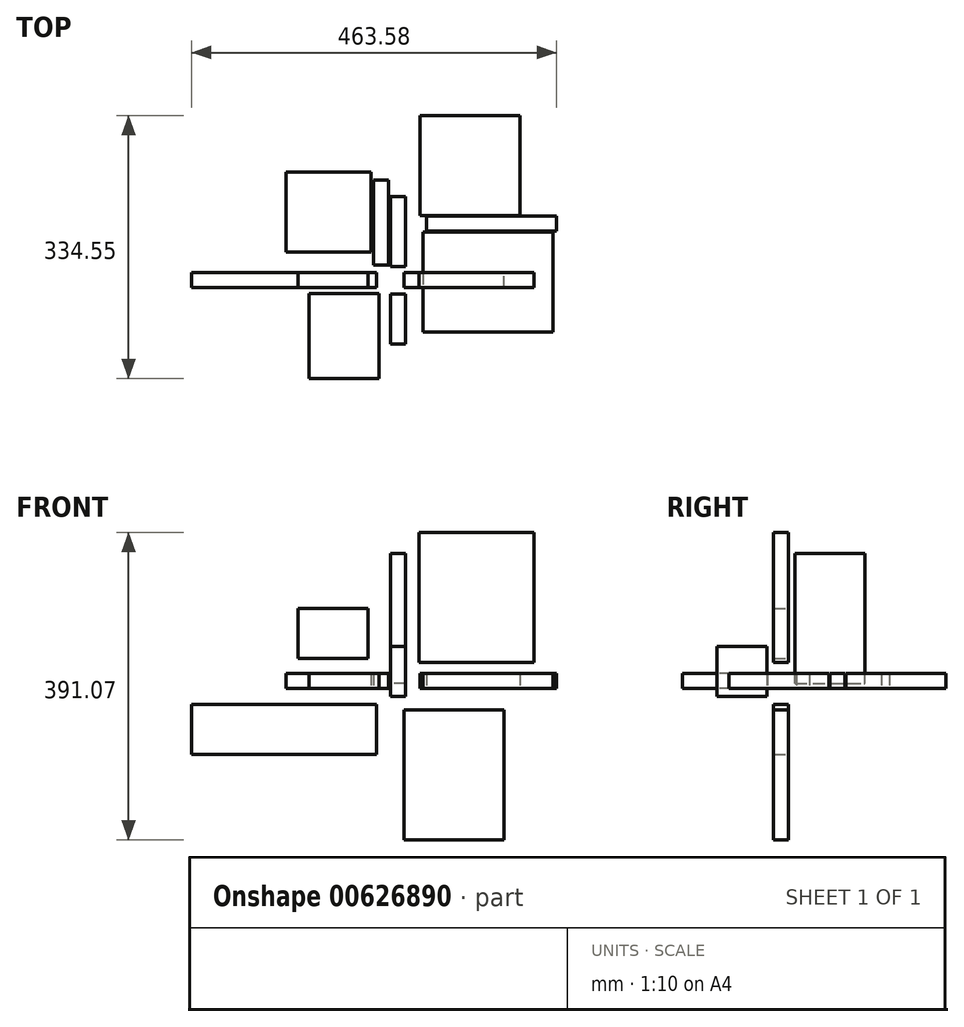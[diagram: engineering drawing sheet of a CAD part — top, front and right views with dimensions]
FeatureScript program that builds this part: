
annotation { "Feature Type Name" : "Feature", "Feature Type Description" : "" }
export const myFeature = defineFeature(function(context is Context, id is Id, definition is map)
    precondition{}
    {
        {
            var Q0;
            Q0=qCreatedBy(makeId("Right.planeOp"),FACE);
            var sketch = newSketch(context, id + "F0", { "sketchPlane" : qUnion([Q0])});
            skLineSegment(sketch, "E0.bottom", {"start": v(8.17, 6.2) * mm, "end": v(97.07, 6.2) * mm});
            skLineSegment(sketch, "E0.top", {"start": v(8.17, 171.3) * mm, "end": v(97.07, 171.3) * mm});
            skLineSegment(sketch, "E0.left", {"start": v(8.17, 6.2) * mm, "end": v(8.17, 171.3) * mm});
            skLineSegment(sketch, "E0.right", {"start": v(97.07, 6.2) * mm, "end": v(97.07, 171.3) * mm});
            skSolve(sketch);
        }
        {
            var Q0;
            Q0 = qSketchRegion(id + "F0", true);
            extrude(context, id + "F1", {"entities" : qUnion([Q0]), "depth" : 19.05 * mm, "offsetDistance" : 25.4 * mm});
        }
        {
            var Q0;
            Q0=qCreatedBy(makeId("Right.planeOp"),FACE);
            var sketch = newSketch(context, id + "F2", { "sketchPlane" : qUnion([Q0])});
            skLineSegment(sketch, "E1.bottom", {"start": v(-27.28, 53.43) * mm, "end": v(-90.78, 53.43) * mm});
            skLineSegment(sketch, "E1.top", {"start": v(-27.28, -10.07) * mm, "end": v(-90.78, -10.07) * mm});
            skLineSegment(sketch, "E1.left", {"start": v(-27.28, 53.43) * mm, "end": v(-27.28, -10.07) * mm});
            skLineSegment(sketch, "E1.right", {"start": v(-90.78, 53.43) * mm, "end": v(-90.78, -10.07) * mm});
            skSolve(sketch);
        }
        {
            var Q0;
            Q0 = qSketchRegion(id + "F2", true);
            extrude(context, id + "F3", {"entities" : qUnion([Q0]), "depth" : 19.05 * mm, "offsetDistance" : 25.4 * mm});
        }
        {
            var Q0;
            Q0=qCreatedBy(makeId("Top.planeOp"),FACE);
            var sketch = newSketch(context, id + "F4", { "sketchPlane" : qUnion([Q0])});
            skLineSegment(sketch, "E2.bottom", {"start": v(36.96, 72.88) * mm, "end": v(163.96, 72.88) * mm});
            skLineSegment(sketch, "E2.top", {"start": v(36.96, 199.88) * mm, "end": v(163.96, 199.88) * mm});
            skLineSegment(sketch, "E2.left", {"start": v(36.96, 72.88) * mm, "end": v(36.96, 199.88) * mm});
            skLineSegment(sketch, "E2.right", {"start": v(163.96, 72.88) * mm, "end": v(163.96, 199.88) * mm});
            skSolve(sketch);
        }
        {
            var Q0;
            Q0 = qSketchRegion(id + "F4", true);
            extrude(context, id + "F5", {"entities" : qUnion([Q0]), "depth" : 19.05 * mm, "offsetDistance" : 25.4 * mm});
        }
        {
            var Q0;
            Q0=qCreatedBy(makeId("Top.planeOp"),FACE);
            var sketch = newSketch(context, id + "F6", { "sketchPlane" : qUnion([Q0])});
            skLineSegment(sketch, "E3.bottom", {"start": v(-25.07, 26.31) * mm, "end": v(-133.02, 26.31) * mm});
            skLineSegment(sketch, "E3.top", {"start": v(-25.07, 127.91) * mm, "end": v(-133.02, 127.91) * mm});
            skLineSegment(sketch, "E3.left", {"start": v(-25.07, 26.31) * mm, "end": v(-25.07, 127.91) * mm});
            skLineSegment(sketch, "E3.right", {"start": v(-133.02, 26.31) * mm, "end": v(-133.02, 127.91) * mm});
            skSolve(sketch);
        }
        {
            var Q0;
            Q0 = qSketchRegion(id + "F6", true);
            extrude(context, id + "F7", {"entities" : qUnion([Q0]), "depth" : 19.05 * mm, "offsetDistance" : 25.4 * mm});
        }
        {
            var Q0;
            Q0=qCreatedBy(makeId("Front.planeOp"),FACE);
            var sketch = newSketch(context, id + "F8", { "sketchPlane" : qUnion([Q0])});
            skLineSegment(sketch, "E4.bottom", {"start": v(-28.65, 37.96) * mm, "end": v(-117.55, 37.96) * mm});
            skLineSegment(sketch, "E4.top", {"start": v(-28.65, 101.46) * mm, "end": v(-117.55, 101.46) * mm});
            skLineSegment(sketch, "E4.left", {"start": v(-28.65, 37.96) * mm, "end": v(-28.65, 101.46) * mm});
            skLineSegment(sketch, "E4.right", {"start": v(-117.55, 37.96) * mm, "end": v(-117.55, 101.46) * mm});
            skSolve(sketch);
        }
        {
            var Q0;
            Q0 = qSketchRegion(id + "F8", true);
            extrude(context, id + "F9", {"entities" : qUnion([Q0]), "depth" : 19.05 * mm, "offsetDistance" : 25.4 * mm});
        }
        {
            var Q0;
            Q0=qCreatedBy(makeId("Front.planeOp"),FACE);
            var sketch = newSketch(context, id + "F10", { "sketchPlane" : qUnion([Q0])});
            skLineSegment(sketch, "E5.bottom", {"start": v(16.7, -27.61) * mm, "end": v(143.7, -27.61) * mm});
            skLineSegment(sketch, "E5.top", {"start": v(16.7, -192.71) * mm, "end": v(143.7, -192.71) * mm});
            skLineSegment(sketch, "E5.left", {"start": v(16.7, -27.61) * mm, "end": v(16.7, -192.71) * mm});
            skLineSegment(sketch, "E5.right", {"start": v(143.7, -27.61) * mm, "end": v(143.7, -192.71) * mm});
            skSolve(sketch);
        }
        {
            var Q0;
            Q0 = qSketchRegion(id + "F10", true);
            extrude(context, id + "F11", {"entities" : qUnion([Q0]), "depth" : 19.05 * mm, "offsetDistance" : 25.4 * mm});
        }
        {
            var Q0;
            Q0=qCreatedBy(makeId("Top.planeOp"),FACE);
            var sketch = newSketch(context, id + "F12", { "sketchPlane" : qUnion([Q0])});
            skLineSegment(sketch, "E6.bottom", {"start": v(40.82, 51.65) * mm, "end": v(205.92, 51.65) * mm});
            skLineSegment(sketch, "E6.top", {"start": v(40.82, -75.35) * mm, "end": v(205.92, -75.35) * mm});
            skLineSegment(sketch, "E6.left", {"start": v(40.82, 51.65) * mm, "end": v(40.82, -75.35) * mm});
            skLineSegment(sketch, "E6.right", {"start": v(205.92, 51.65) * mm, "end": v(205.92, -75.35) * mm});
            skSolve(sketch);
        }
        {
            var Q0;
            Q0 = qSketchRegion(id + "F12", true);
            extrude(context, id + "F13", {"entities" : qUnion([Q0]), "depth" : 19.05 * mm, "offsetDistance" : 25.4 * mm});
        }
        {
            var Q0;
            Q0=qCreatedBy(makeId("Front.planeOp"),FACE);
            var sketch = newSketch(context, id + "F14", { "sketchPlane" : qUnion([Q0])});
            skLineSegment(sketch, "E7.bottom", {"start": v(35.6, 33.26) * mm, "end": v(181.65, 33.26) * mm});
            skLineSegment(sketch, "E7.top", {"start": v(35.6, 198.36) * mm, "end": v(181.65, 198.36) * mm});
            skLineSegment(sketch, "E7.left", {"start": v(35.6, 33.26) * mm, "end": v(35.6, 198.36) * mm});
            skLineSegment(sketch, "E7.right", {"start": v(181.65, 33.26) * mm, "end": v(181.65, 198.36) * mm});
            skSolve(sketch);
        }
        {
            var Q0;
            Q0 = qSketchRegion(id + "F14", true);
            extrude(context, id + "F15", {"entities" : qUnion([Q0]), "depth" : 19.05 * mm, "offsetDistance" : 25.4 * mm});
        }
        {
            var Q0;
            Q0=qCreatedBy(makeId("Front.planeOp"),FACE);
            var sketch = newSketch(context, id + "F16", { "sketchPlane" : qUnion([Q0])});
            skLineSegment(sketch, "E8.bottom", {"start": v(-18.03, -20.28) * mm, "end": v(-252.98, -20.28) * mm});
            skLineSegment(sketch, "E8.top", {"start": v(-18.03, -83.78) * mm, "end": v(-252.98, -83.78) * mm});
            skLineSegment(sketch, "E8.left", {"start": v(-18.03, -20.28) * mm, "end": v(-18.03, -83.78) * mm});
            skLineSegment(sketch, "E8.right", {"start": v(-252.98, -20.28) * mm, "end": v(-252.98, -83.78) * mm});
            skSolve(sketch);
        }
        {
            var Q0;
            Q0 = qSketchRegion(id + "F16", true);
            extrude(context, id + "F17", {"entities" : qUnion([Q0]), "depth" : 19.05 * mm, "offsetDistance" : 25.4 * mm});
        }
        {
            var Q0;
            Q0=qCreatedBy(makeId("Top.planeOp"),FACE);
            var sketch = newSketch(context, id + "F18", { "sketchPlane" : qUnion([Q0])});
            skLineSegment(sketch, "E9.bottom", {"start": v(-15.06, -26.72) * mm, "end": v(-103.96, -26.72) * mm});
            skLineSegment(sketch, "E9.top", {"start": v(-15.06, -134.67) * mm, "end": v(-103.96, -134.67) * mm});
            skLineSegment(sketch, "E9.left", {"start": v(-15.06, -26.72) * mm, "end": v(-15.06, -134.67) * mm});
            skLineSegment(sketch, "E9.right", {"start": v(-103.96, -26.72) * mm, "end": v(-103.96, -134.67) * mm});
            skSolve(sketch);
        }
        {
            var Q0;
            Q0 = qSketchRegion(id + "F18", true);
            extrude(context, id + "F19", {"entities" : qUnion([Q0]), "depth" : 19.05 * mm, "offsetDistance" : 25.4 * mm});
        }
        {
            var Q0;
            Q0=qCreatedBy(makeId("Top.planeOp"),FACE);
            var sketch = newSketch(context, id + "F20", { "sketchPlane" : qUnion([Q0])});
            skLineSegment(sketch, "E10.bottom", {"start": v(45.5, 71.9) * mm, "end": v(210.6, 71.9) * mm});
            skLineSegment(sketch, "E10.top", {"start": v(45.5, 52.85) * mm, "end": v(210.6, 52.85) * mm});
            skLineSegment(sketch, "E10.left", {"start": v(45.5, 71.9) * mm, "end": v(45.5, 52.85) * mm});
            skLineSegment(sketch, "E10.right", {"start": v(210.6, 71.9) * mm, "end": v(210.6, 52.85) * mm});
            skSolve(sketch);
        }
        {
            var Q0;
            Q0 = qSketchRegion(id + "F20", true);
            extrude(context, id + "F21", {"entities" : qUnion([Q0]), "depth" : 19.05 * mm, "offsetDistance" : 25.4 * mm});
        }
        {
            var Q0;
            Q0=qCreatedBy(makeId("Top.planeOp"),FACE);
            var sketch = newSketch(context, id + "F22", { "sketchPlane" : qUnion([Q0])});
            skLineSegment(sketch, "E11.bottom", {"start": v(-2.81, 9.81) * mm, "end": v(-21.86, 9.81) * mm});
            skLineSegment(sketch, "E11.top", {"start": v(-2.81, 117.76) * mm, "end": v(-21.86, 117.76) * mm});
            skLineSegment(sketch, "E11.left", {"start": v(-2.81, 9.81) * mm, "end": v(-2.81, 117.76) * mm});
            skLineSegment(sketch, "E11.right", {"start": v(-21.86, 9.81) * mm, "end": v(-21.86, 117.76) * mm});
            skSolve(sketch);
        }
        {
            var Q0;
            Q0 = qSketchRegion(id + "F22", true);
            extrude(context, id + "F23", {"entities" : qUnion([Q0]), "depth" : 19.05 * mm, "offsetDistance" : 25.4 * mm});
        }
    });
